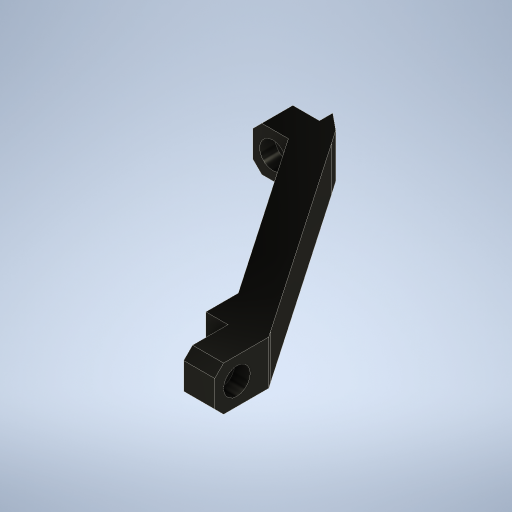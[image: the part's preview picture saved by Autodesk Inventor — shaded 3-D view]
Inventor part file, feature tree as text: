
AUTODESK INVENTOR PART (.ipt)
format: ipt  version: 2024.3 (Build 283343000, 343)  size: 317,952 bytes
history: native  units: mm
features: extrude x7, sketch x7, chamfer x1
ambient origin geometry x8: Origin, YZ Plane, XZ Plane, XY Plane, X Axis, Y Axis, Z Axis, Center Point
bodies: Solid1 (feature_tree)
feature tree (15):
  extrude  "Extrusion1"  Depth=7.0mm
  chamfer  "Chamfer1"  Distance=10.0mm
  extrude  "Extrusion2"  Depth=7.0mm
  extrude  "Extrusion3"  Depth=7.0mm
  extrude  "Extrusion4"  Depth=10.0mm
  extrude  "Extrusion5"  Depth=10.0mm
  extrude  "Extrusion6"  TaperAngle=135.0deg  [1 undecoded]
  extrude  "Extrusion7"  Depth=3.5mm
  sketch  "Sketch1"  dims[d0=10.0mm d1=7.0mm]
  sketch  "Sketch2"  dims[d7=29.5mm d12=10.0mm d13=0.0mm]
  sketch  "Sketch3"  dims[d14=50.1mm d15=7.0mm]
  sketch  "Sketch4"  dims[d16=8.0mm d17=7.0mm]
  sketch  "Sketch5"  dims[d18=2.0mm d19=2.0mm d20=45.0deg d21=10.0mm]
  sketch  "Sketch6"  dims[d22=10.0mm d23=3.2mm]
  sketch  "Sketch7"  dims[d24=0.0mm d25=0.0mm d26=135.0deg d27=3.5mm d28=3.0mm d29=10.0mm d30=0.0mm d31=6.0mm d32=3.5mm d33=0.0mm d34=6.0mm d35=3.5mm d36=0.0mm d37=5.0mm d38=90.0deg d39=10.0mm d40=0.0mm d41=3.662mm d42=3.0mm d43=10.0mm d44=0.0mm]
note: 1 required parameter value undecoded (feature->parameter linkage not recoverable at this tier; creation-order binding heuristic only, values carry confidence <= 0.55)
